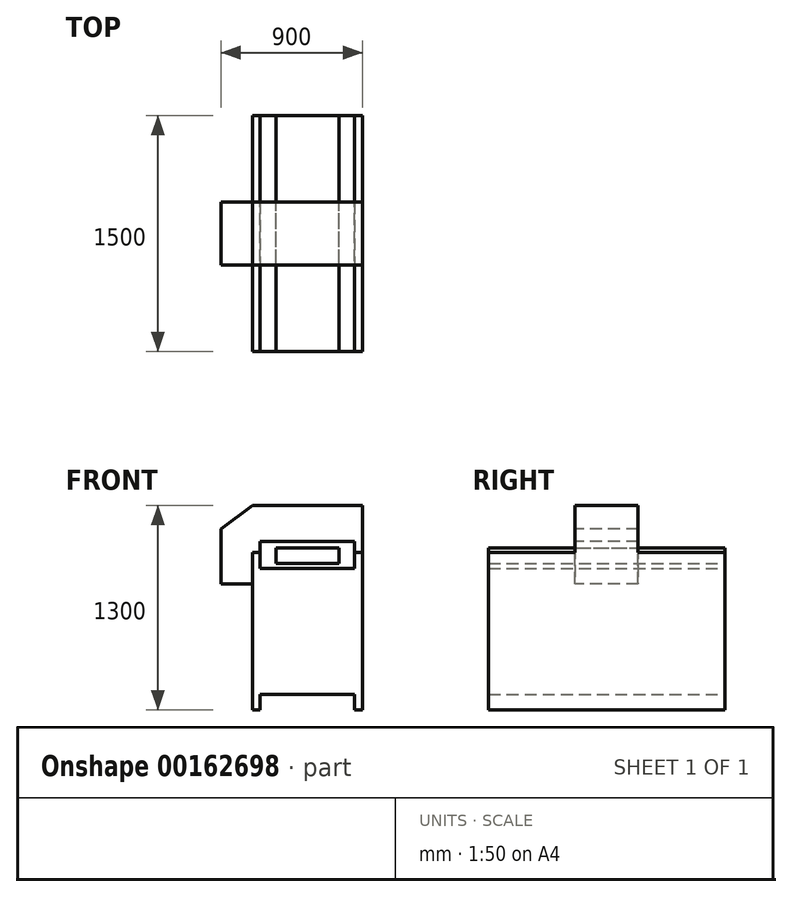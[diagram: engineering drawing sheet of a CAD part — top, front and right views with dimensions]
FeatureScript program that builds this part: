
annotation { "Feature Type Name" : "Feature", "Feature Type Description" : "" }
export const myFeature = defineFeature(function(context is Context, id is Id, definition is map)
    precondition{}
    {
        {
            var Q0;
            Q0=qCreatedBy(makeId("Front.planeOp"),FACE);
            var sketch = newSketch(context, id + "F0", { "sketchPlane" : qUnion([Q0])});
            skLineSegment(sketch, "E0", {"start": v(0, 0) * mm, "end": v(0, 1000) * mm});
            skLineSegment(sketch, "E1", {"start": v(0, 1000) * mm, "end": v(50, 1000) * mm});
            skLineSegment(sketch, "E2", {"start": v(50, 1000) * mm, "end": v(50, 900) * mm});
            skLineSegment(sketch, "E3", {"start": v(50, 900) * mm, "end": v(650, 900) * mm});
            skLineSegment(sketch, "E4", {"start": v(650, 900) * mm, "end": v(650, 1000) * mm});
            skLineSegment(sketch, "E5", {"start": v(650, 1000) * mm, "end": v(700, 1000) * mm});
            skLineSegment(sketch, "E6", {"start": v(700, 1000) * mm, "end": v(700, 0) * mm});
            skLineSegment(sketch, "E7", {"start": v(700, 0) * mm, "end": v(650, 0) * mm});
            skLineSegment(sketch, "E8", {"start": v(650, 0) * mm, "end": v(650, 100) * mm});
            skLineSegment(sketch, "E9", {"start": v(650, 100) * mm, "end": v(50, 100) * mm});
            skLineSegment(sketch, "E10", {"start": v(50, 100) * mm, "end": v(50, 0) * mm});
            skLineSegment(sketch, "E11", {"start": v(50, 0) * mm, "end": v(0, 0) * mm});
            skLineSegment(sketch, "E12.bottom", {"start": v(550, 1030) * mm, "end": v(150, 1030) * mm});
            skLineSegment(sketch, "E12.top", {"start": v(550, 930) * mm, "end": v(150, 930) * mm});
            skLineSegment(sketch, "E12.left", {"start": v(550, 1030) * mm, "end": v(550, 930) * mm});
            skLineSegment(sketch, "E12.right", {"start": v(150, 1030) * mm, "end": v(150, 930) * mm});
            skSolve(sketch);
        }
        {
            var Q0;
            Q0 = qSketchRegion(id + "F0", true);
            extrude(context, id + "F1", {"entities" : qUnion([Q0]), "depth" : 1500 * mm});
        }
        {
            var Q0;
            Q0=makeQuery(id+"F1.opExtrude","CAP_FACE",FACE,{"disambiguationData":[OSD([sQuery(id+"F0.wireOp",EDGE,"E0"),sQuery(id+"F0.wireOp",EDGE,"E1"),sQuery(id+"F0.wireOp",EDGE,"E2"),sQuery(id+"F0.wireOp",EDGE,"E3"),sQuery(id+"F0.wireOp",EDGE,"E4"),sQuery(id+"F0.wireOp",EDGE,"E5"),sQuery(id+"F0.wireOp",EDGE,"E6"),sQuery(id+"F0.wireOp",EDGE,"E7"),sQuery(id+"F0.wireOp",EDGE,"E8"),sQuery(id+"F0.wireOp",EDGE,"E9"),sQuery(id+"F0.wireOp",EDGE,"E10"),sQuery(id+"F0.wireOp",EDGE,"E11")])],"isStart":false});
            cPlane(context, id + "F2", {"entities" : qUnion([Q0]), "cplaneType" : CPlaneType.OFFSET, "offset" : 550 * mm, "oppositeDirection" : true, "width" : 150 * mm, "height" : 150 * mm});
        }
        {
            var Q0;
            Q0=qCreatedBy(id+"F2.planeOp",FACE);
            var sketch = newSketch(context, id + "F3", { "sketchPlane" : qUnion([Q0])});
            skLineSegment(sketch, "E13", {"start": v(50, 1000) * mm, "end": v(50, 1070) * mm});
            skLineSegment(sketch, "E14", {"start": v(50, 1070) * mm, "end": v(650, 1070) * mm});
            skLineSegment(sketch, "E15", {"start": v(650, 1070) * mm, "end": v(650, 1000) * mm});
            skLineSegment(sketch, "E16", {"start": v(650, 1000) * mm, "end": v(700, 1000) * mm});
            skLineSegment(sketch, "E17", {"start": v(700, 1000) * mm, "end": v(700, 1300) * mm});
            skLineSegment(sketch, "E18", {"start": v(700, 1300) * mm, "end": v(0, 1300) * mm});
            skLineSegment(sketch, "E19", {"start": v(0, 1300) * mm, "end": v(-200, 1150) * mm});
            skLineSegment(sketch, "E20", {"start": v(-200, 1150) * mm, "end": v(-200, 800) * mm});
            skLineSegment(sketch, "E21", {"start": v(-200, 800) * mm, "end": v(0, 800) * mm});
            skLineSegment(sketch, "E22", {"start": v(0, 800) * mm, "end": v(0, 1000) * mm});
            skLineSegment(sketch, "E23", {"start": v(0, 1000) * mm, "end": v(50, 1000) * mm});
            skSolve(sketch);
        }
        {
            var Q0;
            Q0 = qSketchRegion(id + "F3", true);
            extrude(context, id + "F4", {"entities" : qUnion([Q0]), "operationType" : NewBodyOperationType.ADD, "oppositeDirection" : true, "depth" : 400 * mm});
        }
    });
